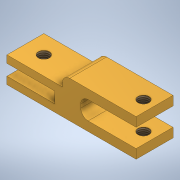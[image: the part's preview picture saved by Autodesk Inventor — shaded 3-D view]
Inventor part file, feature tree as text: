
AUTODESK INVENTOR PART (.ipt)
format: ipt  version: 2020 (Build 240168000, 168)  size: 165,888 bytes
history: native  units: mm
features: thread x4, hole x3, plane x2, sketch x2, extrude x1
ambient origin geometry x8: Origin, YZ Plane, XZ Plane, XY Plane, X Axis, Y Axis, Z Axis, Center Point
bodies: Body1 (feature_tree)
feature tree (12):
  plane  "Work Plane1"
  plane  "Work Plane5"
  sketch  "Sketch5"  dims[d42=-25.0mm d61=15.0mm d66=5.0mm]
  hole  "Hole1"  [1 undecoded]
  extrude  "Extrusion5"  Depth=2.5mm
  hole  "Hole2"  [1 undecoded]
  hole  "Hole3"  [1 undecoded]
  thread  "Thread1"  [1 undecoded]
  thread  "Thread2"  [1 undecoded]
  thread  "Thread3"  [1 undecoded]
  thread  "Thread4"  [1 undecoded]
  sketch  "Sketch8"  dims[d67=2.5mm d68=2.5mm d69=20.0mm d70=15.0mm d71=2.0mm d79=3.0mm d80=6.0mm d81=4.0mm d82=2.0mm d83=90.0deg d84=8.0mm d85=20.594885mm d86=3.0mm d87=5.0mm d111=2.0mm d112=2.0mm d113=3.0mm d115=2.0mm d116=15.0mm d117=15.0mm d118=10.0mm d119=0.0mm d120=3.0mm d121=6.0mm d122=4.0mm d123=2.0mm d124=90.0deg d125=8.0mm d126=20.594885mm d127=5.0mm d128=5.0mm d129=3.0mm d130=6.0mm d131=4.0mm d132=2.0mm d133=90.0deg d134=8.0mm d135=20.594885mm d136=2.0mm d137=0.0mm d138=2.5mm d139=0.0mm d140=2.5mm d141=0.0mm d142=2.0mm d143=0.0mm d57=0.5mm d58=0.872665mm d59=0.5mm d60=0.872665mm]
note: 7 required parameter values undecoded (feature->parameter linkage not recoverable at this tier; creation-order binding heuristic only, values carry confidence <= 0.55)
